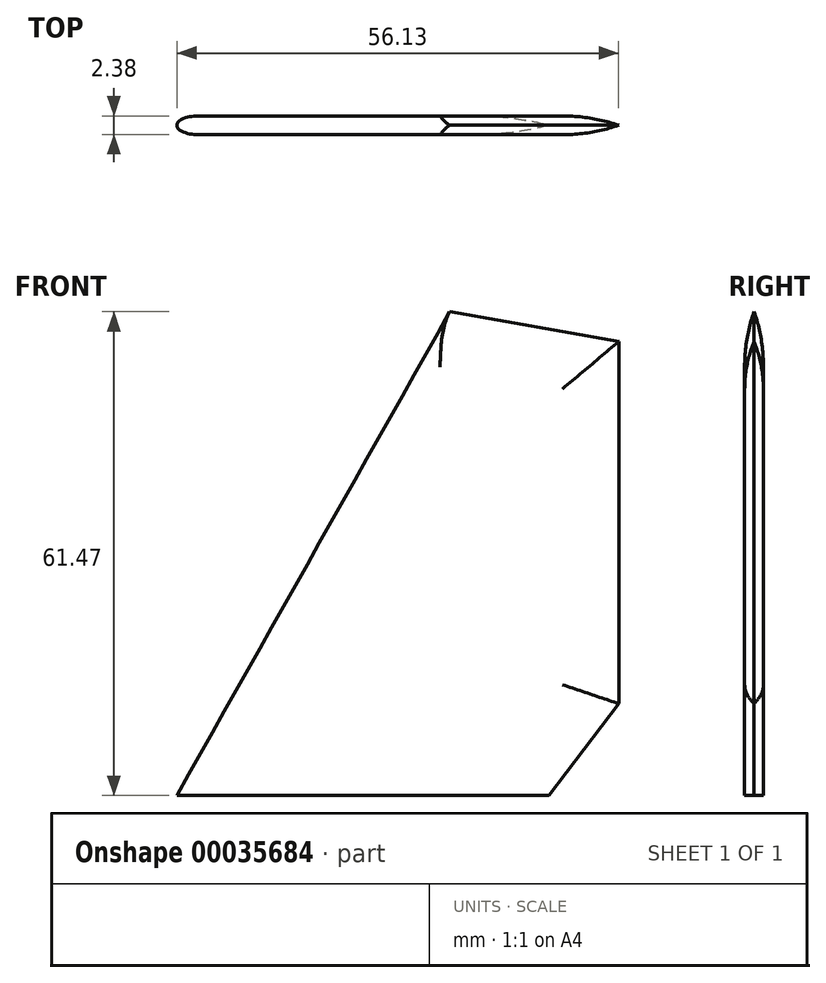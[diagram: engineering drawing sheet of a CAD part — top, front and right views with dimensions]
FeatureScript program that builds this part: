
annotation { "Feature Type Name" : "Feature", "Feature Type Description" : "" }
export const myFeature = defineFeature(function(context is Context, id is Id, definition is map)
    precondition{}
    {
        {
            var Q0;
            Q0=qCreatedBy(makeId("Front.planeOp"),FACE);
            var sketch = newSketch(context, id + "F0", { "sketchPlane" : qUnion([Q0])});
            skLineSegment(sketch, "E0", {"start": v(0, 0) * mm, "end": v(43.69, 77.47) * mm});
            skLineSegment(sketch, "E1", {"start": v(43.69, 77.47) * mm, "end": v(68.07, 73.15) * mm});
            skLineSegment(sketch, "E2", {"start": v(68.07, 73.15) * mm, "end": v(68.07, 11.68) * mm});
            skLineSegment(sketch, "E3", {"start": v(59.18, 0) * mm, "end": v(0, 0) * mm});
            skLineSegment(sketch, "E4", {"start": v(61.47, 64.82) * mm, "end": v(61.47, 11.68) * mm});
            skLineSegment(sketch, "E5", {"start": v(68.07, 11.68) * mm, "end": v(6.59, 11.68) * mm, "construction": true});
            skLineSegment(sketch, "E6", {"start": v(38.82, 68.83) * mm, "end": v(61.47, 64.82) * mm});
            skLineSegment(sketch, "E7", {"start": v(34.66, 61.47) * mm, "end": v(56.13, 57.67) * mm});
            skLineSegment(sketch, "E8", {"start": v(56.13, 57.67) * mm, "end": v(56.13, 11.68) * mm});
            skLineSegment(sketch, "E9", {"start": v(56.13, 11.68) * mm, "end": v(47.24, 0) * mm});
            skLineSegment(sketch, "E10", {"start": v(68.07, 11.68) * mm, "end": v(59.18, 0) * mm});
            skLineSegment(sketch, "E11", {"start": v(61.47, 11.68) * mm, "end": v(52.58, 0) * mm});
            skSolve(sketch);
        }
        {
            var Q0;
            {var subQ1=sQuery(id+"F0.wireOp",EDGE,"E7");Q0=makeQuery(id+"F0.imprint","IMPRINT",FACE,{"disambiguationData":[TD([[makeQuery(id+"F0.imprint","IMPRINT",EDGE,{"derivedFrom":subQ1}),-1.0]])]});}
            extrude(context, id + "F1", {"entities" : qUnion([Q0]), "depth" : 2.38 * mm, "symmetric" : true});
        }
        {
            var Q0;
            Q0=sQuery(id+"F0.wireOp",EDGE,"E0");
            var Q1;
            Q1=sQuery(id+"F0.wireOp",VERTEX,"E3.end");
            cPlane(context, id + "F2", {"entities" : qUnion([Q0, Q1]), "cplaneType" : CPlaneType.LINE_POINT, "offset" : 152.4 * mm, "width" : 152.4 * mm, "height" : 152.4 * mm});
        }
        {
            var Q0;
            Q0=qCreatedBy(id+"F2.planeOp",FACE);
            var sketch = newSketch(context, id + "F3", { "sketchPlane" : qUnion([Q0])});
            skLineSegment(sketch, "E12.1", {"start": v(2.38, 1.2) * mm, "end": v(20.57, 1.2) * mm});
            skLineSegment(sketch, "E12.2", {"start": v(2.38, -1.2) * mm, "end": v(20.57, -1.2) * mm});
            skLineSegment(sketch, "E13", {"start": v(20.57, 12.7) * mm, "end": v(-12.7, 12.7) * mm});
            skPoint(sketch, "E14.orphan", {"position": v(0, 1.2) * mm});
            skLineSegment(sketch, "E15", {"start": v(-12.7, 12.7) * mm, "end": v(-12.7, -12.7) * mm});
            skLineSegment(sketch, "E16", {"start": v(-12.7, -12.7) * mm, "end": v(20.57, -12.7) * mm});
            skLineSegment(sketch, "E17", {"start": v(20.57, 1.2) * mm, "end": v(20.57, 12.7) * mm});
            skLineSegment(sketch, "E18", {"start": v(20.57, -12.7) * mm, "end": v(20.57, -1.2) * mm});
            skLineSegment(sketch, "E19", {"start": v(2.38, 1.2) * mm, "end": v(2.38, -1.2) * mm, "construction": true});
            skEllipticalArc(sketch, "E20", {});
            skLineSegment(sketch, "E21", {"start": v(0, 0) * mm, "end": v(2.38, 0) * mm});
            skLineSegment(sketch, "E22", {"start": v(2.38, 0) * mm, "end": v(0, 0) * mm, "construction": true});
            const initialGuessF3  = {"E20": [0.002381250000000021, 0, -1, 0, 0.00238125, 0.001190625, 4.71238898038469, 1.5707963267948966]};
            skSetInitialGuess(sketch, initialGuessF3);
            skSolve(sketch);
        }
        {
            var Q0;
            {var subQ3=sQuery(id+"F3.wireOp",EDGE,"E12.1");Q0=makeQuery(id+"F3.imprint","IMPRINT",FACE,{"disambiguationData":[TD([[makeQuery(id+"F3.imprint","IMPRINT",EDGE,{"derivedFrom":subQ3}),1.0]])]});}
            extrude(context, id + "F4", {"entities" : qUnion([Q0]), "operationType" : NewBodyOperationType.REMOVE, "endBound" : BoundingType.THROUGH_ALL, "depth" : 25.4 * mm});
        }
        {
            var Q0;
            Q0=sQuery(id+"F0.wireOp",EDGE,"E9");
            var Q1;
            Q1=sQuery(id+"F0.wireOp",VERTEX,"E9.end");
            cPlane(context, id + "F5", {"entities" : qUnion([Q0, Q1]), "cplaneType" : CPlaneType.LINE_POINT, "offset" : 152.4 * mm, "width" : 152.4 * mm, "height" : 152.4 * mm});
        }
        {
            var Q0;
            Q0=qCreatedBy(id+"F5.planeOp",FACE);
            var sketch = newSketch(context, id + "F6", { "sketchPlane" : qUnion([Q0])});
            skLineSegment(sketch, "E23.0", {"start": v(9.76, -1.2) * mm, "end": v(37.6, -1.2) * mm, "construction": true});
            skLineSegment(sketch, "E24.0", {"start": v(9.76, 1.2) * mm, "end": v(37.6, 1.2) * mm, "construction": true});
            skLineSegment(sketch, "E25.0", {"start": v(37.6, 1.2) * mm, "end": v(37.6, -1.2) * mm, "construction": true});
            skArc(sketch, "E26", {"start": v(30.45, -1.2) * mm, "mid": v(34.08, -0.9) * mm, "end": v(37.6, 0) * mm});
            skPoint(sketch, "E26.startSnap0", {"position": v(37.6, 0) * mm});
            skPoint(sketch, "E27.orphan", {"position": v(23.31, 0) * mm});
            skLineSegment(sketch, "E28", {"start": v(30.45, -1.2) * mm, "end": v(30.45, -3.73) * mm});
            skLineSegment(sketch, "E29", {"start": v(30.45, -3.73) * mm, "end": v(40.14, -3.73) * mm});
            skLineSegment(sketch, "E30", {"start": v(40.14, -3.73) * mm, "end": v(40.14, 3.73) * mm});
            skLineSegment(sketch, "E31", {"start": v(40.14, 3.73) * mm, "end": v(30.45, 3.73) * mm});
            skLineSegment(sketch, "E32", {"start": v(30.45, 3.73) * mm, "end": v(30.45, 1.2) * mm});
            skArc(sketch, "E33.MirrorCS", {"start": v(30.45, 1.2) * mm, "mid": v(34.08, 0.9) * mm, "end": v(37.6, 0) * mm});
            skSolve(sketch);
        }
        {
            var Q0;
            Q0=makeQuery(id+"F6.imprint","IMPRINT",FACE,{"disambiguationData":[TD([[makeQuery(id+"F6.imprint","IMPRINT",EDGE,{"derivedFrom":sQuery(id+"F6.wireOp",EDGE,"E26")}),-1.0]])]});
            extrude(context, id + "F7", {"entities" : qUnion([Q0]), "operationType" : NewBodyOperationType.REMOVE, "oppositeDirection" : true, "depth" : 76.2 * mm, "symmetric" : true});
        }
        {
            var Q0;
            Q0=qCreatedBy(makeId("Top.planeOp"),FACE);
            var sketch = newSketch(context, id + "F8", { "sketchPlane" : qUnion([Q0])});
            skPoint(sketch, "E34.orphan", {"position": v(41.85, 0) * mm});
            skPoint(sketch, "E35.startSnap0", {"position": v(56.13, 0) * mm});
            skLineSegment(sketch, "E36.0", {"start": v(34.66, 1.2) * mm, "end": v(56.13, 1.2) * mm, "construction": true});
            skLineSegment(sketch, "E37.0", {"start": v(34.66, -1.2) * mm, "end": v(56.13, -1.2) * mm, "construction": true});
            skLineSegment(sketch, "E38", {"start": v(49, -3.73) * mm, "end": v(58.67, -3.73) * mm});
            skLineSegment(sketch, "E39", {"start": v(58.67, -3.73) * mm, "end": v(58.67, 3.73) * mm});
            skArc(sketch, "E40.MirrorCS", {"start": v(49, 1.2) * mm, "mid": v(52.61, 0.9) * mm, "end": v(56.13, 0) * mm});
            skLineSegment(sketch, "E41", {"start": v(58.67, 3.73) * mm, "end": v(49, 3.73) * mm});
            skArc(sketch, "E35", {"start": v(49, -1.2) * mm, "mid": v(52.61, -0.9) * mm, "end": v(56.13, 0) * mm});
            skLineSegment(sketch, "E42.0", {"start": v(56.13, 1.2) * mm, "end": v(56.13, -1.2) * mm, "construction": true});
            skLineSegment(sketch, "E43", {"start": v(34.66, -1.2) * mm, "end": v(34.66, 0) * mm});
            skLineSegment(sketch, "E44", {"start": v(34.66, 0) * mm, "end": v(34.66, 1.2) * mm});
            skLineSegment(sketch, "E45", {"start": v(49, -3.73) * mm, "end": v(49, -1.2) * mm});
            skLineSegment(sketch, "E46", {"start": v(49, 1.2) * mm, "end": v(49, 3.73) * mm});
            skLineSegment(sketch, "E47", {"start": v(49, -1.2) * mm, "end": v(49, 1.2) * mm, "construction": true});
            skSolve(sketch);
        }
        {
            var Q0;
            Q0=makeQuery(id+"F8.imprint","IMPRINT",FACE,{"disambiguationData":[TD([[makeQuery(id+"F8.imprint","IMPRINT",EDGE,{"derivedFrom":sQuery(id+"F8.wireOp",EDGE,"E38")}),1.0]])]});
            extrude(context, id + "F9", {"entities" : qUnion([Q0]), "operationType" : NewBodyOperationType.REMOVE, "endBound" : BoundingType.THROUGH_ALL, "depth" : 25.4 * mm});
        }
        {
            var Q0;
            Q0=sQuery(id+"F0.wireOp",EDGE,"E7");
            var Q1;
            Q1=sQuery(id+"F0.wireOp",VERTEX,"E7.end");
            cPlane(context, id + "F10", {"entities" : qUnion([Q0, Q1]), "cplaneType" : CPlaneType.LINE_POINT, "offset" : 152.4 * mm, "width" : 152.4 * mm, "height" : 152.4 * mm});
        }
        {
            var Q0;
            Q0=qCreatedBy(id+"F10.planeOp",FACE);
            var sketch = newSketch(context, id + "F11", { "sketchPlane" : qUnion([Q0])});
            skLineSegment(sketch, "E48.0", {"start": v(-1.2, 66.57) * mm, "end": v(-1.2, 22.42) * mm, "construction": true});
            skLineSegment(sketch, "E49.0", {"start": v(1.2, 66.57) * mm, "end": v(1.2, 22.42) * mm, "construction": true});
            skLineSegment(sketch, "E50.0", {"start": v(0, 66.57) * mm, "end": v(-1.2, 66.57) * mm, "construction": true});
            skLineSegment(sketch, "E51.0", {"start": v(0, 66.57) * mm, "end": v(1.2, 66.57) * mm, "construction": true});
            skArc(sketch, "E52", {"start": v(0, 66.57) * mm, "mid": v(-0.9, 63.05) * mm, "end": v(-1.2, 59.43) * mm});
            skLineSegment(sketch, "E53", {"start": v(-1.2, 59.43) * mm, "end": v(-3.73, 59.43) * mm});
            skPoint(sketch, "E53.endSnap0", {"position": v(-1.2, 59.43) * mm});
            skLineSegment(sketch, "E54", {"start": v(-3.73, 59.43) * mm, "end": v(-3.73, 69.11) * mm});
            skLineSegment(sketch, "E55", {"start": v(-3.73, 69.11) * mm, "end": v(0, 69.11) * mm});
            skPoint(sketch, "E56.orphan", {"position": v(0, 52.28) * mm});
            skLineSegment(sketch, "E57.MirrorCS", {"start": v(3.73, 69.11) * mm, "end": v(0, 69.11) * mm});
            skLineSegment(sketch, "E58.MirrorCS", {"start": v(3.73, 59.43) * mm, "end": v(3.73, 69.11) * mm});
            skLineSegment(sketch, "E59.MirrorCS", {"start": v(1.2, 59.43) * mm, "end": v(3.73, 59.43) * mm});
            skArc(sketch, "E60.MirrorCS", {"start": v(0, 66.57) * mm, "mid": v(0.9, 63.05) * mm, "end": v(1.2, 59.43) * mm});
            skSolve(sketch);
        }
        {
            var Q0;
            Q0=makeQuery(id+"F11.imprint","IMPRINT",FACE,{"disambiguationData":[TD([[makeQuery(id+"F11.imprint","IMPRINT",EDGE,{"derivedFrom":sQuery(id+"F11.wireOp",EDGE,"E52")}),-1.0]])]});
            extrude(context, id + "F12", {"entities" : qUnion([Q0]), "operationType" : NewBodyOperationType.REMOVE, "oppositeDirection" : true, "depth" : 76.2 * mm, "symmetric" : true});
        }
    });
